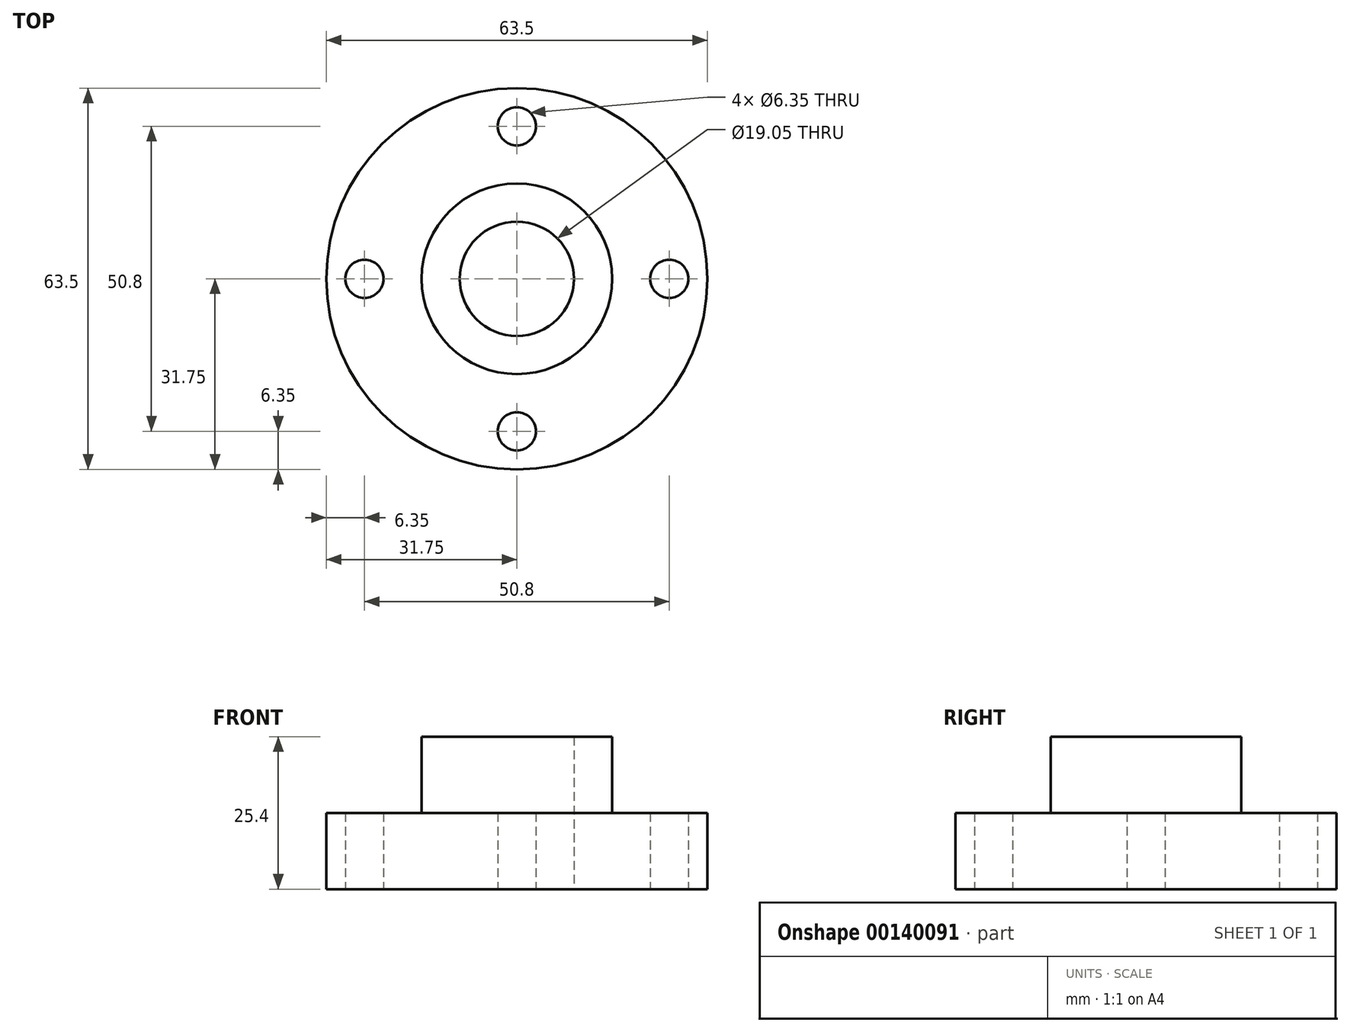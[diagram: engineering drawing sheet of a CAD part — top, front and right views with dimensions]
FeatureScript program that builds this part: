
annotation { "Feature Type Name" : "Feature", "Feature Type Description" : "" }
export const myFeature = defineFeature(function(context is Context, id is Id, definition is map)
    precondition{}
    {
        {
            var Q0;
            Q0=qCreatedBy(makeId("Top.planeOp"),FACE);
            var sketch = newSketch(context, id + "F0", { "sketchPlane" : qUnion([Q0])});
            skCircle(sketch, "E0", {"center": v(0, 0) * mm, "radius": 9.53 * mm});
            skCircle(sketch, "E1", {"center": v(0, 0) * mm, "radius": 15.88 * mm});
            skCircle(sketch, "E2", {"center": v(0, 0) * mm, "radius": 25.4 * mm});
            skCircle(sketch, "E3", {"center": v(0, 0) * mm, "radius": 31.75 * mm});
            skCircle(sketch, "E4", {"center": v(0, 25.4) * mm, "radius": 3.18 * mm});
            skCircle(sketch, "E5", {"center": v(25.4, 0) * mm, "radius": 3.18 * mm});
            skCircle(sketch, "E6", {"center": v(0, -25.4) * mm, "radius": 3.18 * mm});
            skCircle(sketch, "E7", {"center": v(-25.4, 0) * mm, "radius": 3.18 * mm});
            skSolve(sketch);
        }
        {
            var Q0;
            Q0=makeQuery(id+"F0.imprint","IMPRINT",FACE,{"disambiguationData":[TD([[makeQuery(id+"F0.imprint","IMPRINT",EDGE,{"derivedFrom":sQuery(id+"F0.wireOp",EDGE,"E0")}),-1.0]])]});
            extrude(context, id + "F1", {"entities" : qUnion([Q0]), "depth" : 25.4 * mm});
        }
        {
            var Q0;
            Q0=makeQuery(id+"F0.imprint","IMPRINT",FACE,{"disambiguationData":[TD([[makeQuery(id+"F0.imprint","IMPRINT",EDGE,{"derivedFrom":sQuery(id+"F0.wireOp",EDGE,"E3")}),1.0]])]});
            var Q1;
            Q1=makeQuery(id+"F0.imprint","IMPRINT",FACE,{"disambiguationData":[TD([[makeQuery(id+"F0.imprint","IMPRINT",EDGE,{"derivedFrom":sQuery(id+"F0.wireOp",EDGE,"E1")}),-1.0]])]});
            extrude(context, id + "F2", {"entities" : qUnion([Q0, Q1]), "operationType" : NewBodyOperationType.ADD, "depth" : 12.7 * mm});
        }
    });
